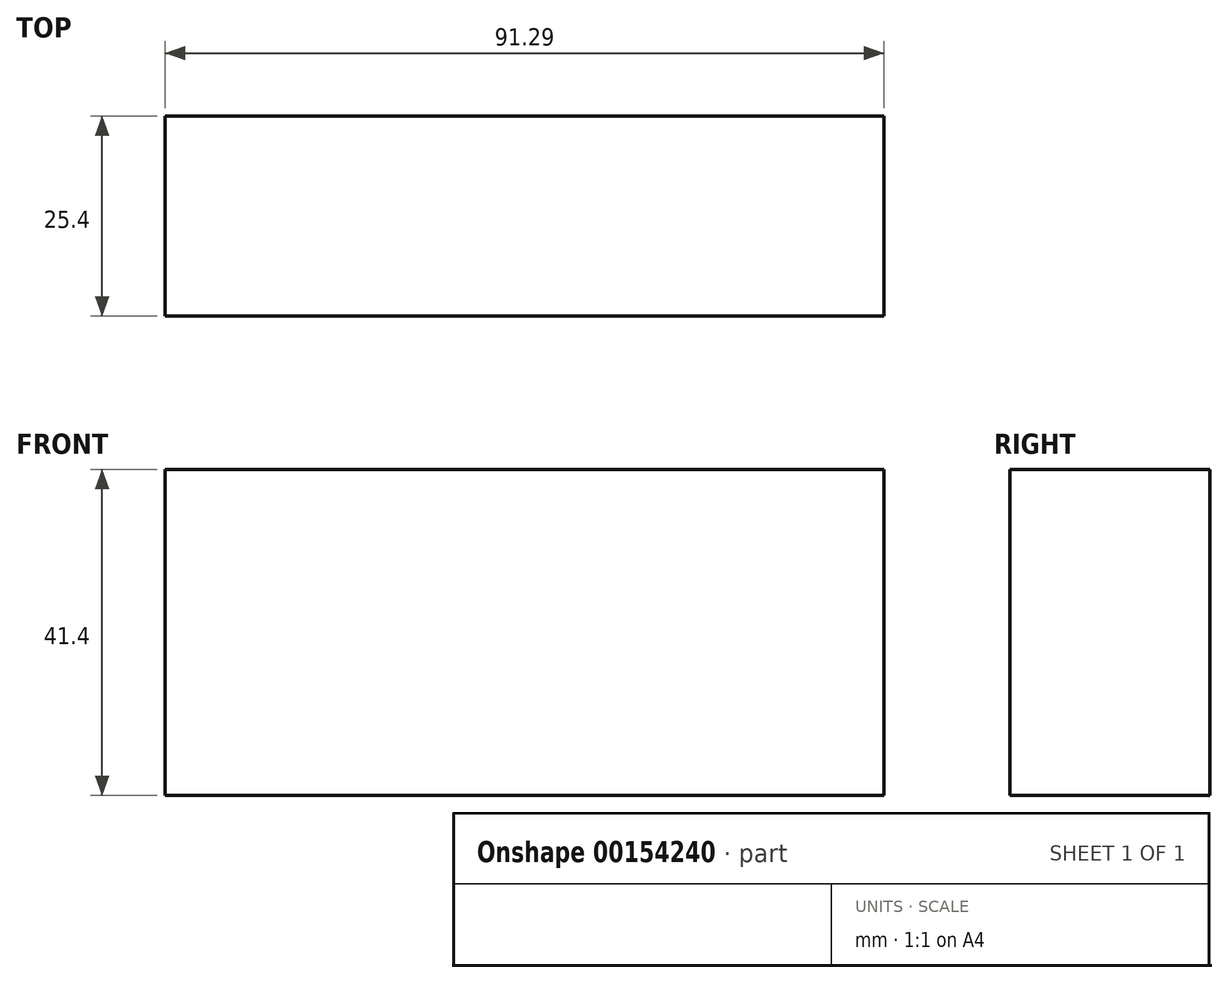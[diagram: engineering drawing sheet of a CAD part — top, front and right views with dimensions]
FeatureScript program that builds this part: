
annotation { "Feature Type Name" : "Feature", "Feature Type Description" : "" }
export const myFeature = defineFeature(function(context is Context, id is Id, definition is map)
    precondition{}
    {
        {
            var Q0;
            Q0=qCreatedBy(makeId("Front.planeOp"),FACE);
            var sketch = newSketch(context, id + "F0", { "sketchPlane" : qUnion([Q0])});
            skLineSegment(sketch, "E0.bottom", {"start": v(-29.45, 22.81) * mm, "end": v(61.84, 22.81) * mm});
            skLineSegment(sketch, "E0.top", {"start": v(-29.45, -18.59) * mm, "end": v(61.84, -18.59) * mm});
            skLineSegment(sketch, "E0.left", {"start": v(-29.45, 22.81) * mm, "end": v(-29.45, -18.59) * mm});
            skLineSegment(sketch, "E0.right", {"start": v(61.84, 22.81) * mm, "end": v(61.84, -18.59) * mm});
            skLineSegment(sketch, "E1.bottom", {"start": v(61.84, 22.81) * mm, "end": v(58.66, 22.81) * mm});
            skLineSegment(sketch, "E1.top", {"start": v(61.84, -18.59) * mm, "end": v(58.66, -18.59) * mm});
            skLineSegment(sketch, "E1.right", {"start": v(58.66, 22.81) * mm, "end": v(58.66, -18.59) * mm});
            skLineSegment(sketch, "E2.bottom", {"start": v(-29.45, 22.81) * mm, "end": v(-26.27, 22.81) * mm});
            skLineSegment(sketch, "E2.top", {"start": v(-29.45, -18.59) * mm, "end": v(-26.27, -18.59) * mm});
            skLineSegment(sketch, "E2.right", {"start": v(-26.27, 22.81) * mm, "end": v(-26.27, -18.59) * mm});
            skSolve(sketch);
        }
        {
            var Q0;
            Q0 = qSketchRegion(id + "F0", true);
            extrude(context, id + "F1", {"entities" : qUnion([Q0]), "depth" : 25.4 * mm});
        }
    });
